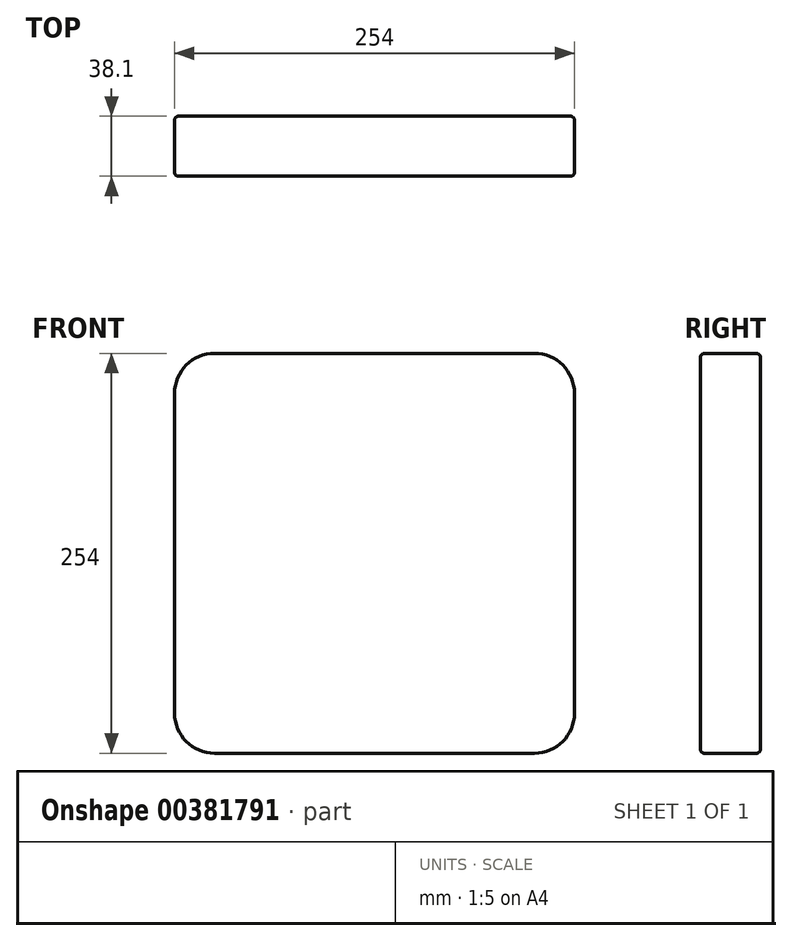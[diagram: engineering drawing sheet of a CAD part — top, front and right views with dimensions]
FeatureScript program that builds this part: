
annotation { "Feature Type Name" : "Feature", "Feature Type Description" : "" }
export const myFeature = defineFeature(function(context is Context, id is Id, definition is map)
    precondition{}
    {
        {
            var Q0;
            Q0=qCreatedBy(makeId("Front.planeOp"),FACE);
            var sketch = newSketch(context, id + "F0", { "sketchPlane" : qUnion([Q0])});
            skLineSegment(sketch, "E0.bottom", {"start": v(0, 0) * mm, "end": v(254, 0) * mm});
            skLineSegment(sketch, "E0.top", {"start": v(0, 254) * mm, "end": v(254, 254) * mm});
            skLineSegment(sketch, "E0.left", {"start": v(0, 0) * mm, "end": v(0, 254) * mm});
            skLineSegment(sketch, "E0.right", {"start": v(254, 0) * mm, "end": v(254, 254) * mm});
            skSolve(sketch);
        }
        {
            var Q0;
            Q0=makeQuery(id+"F0.imprint","IMPRINT",FACE,{"disambiguationData":[TD([[makeQuery(id+"F0.imprint","IMPRINT",EDGE,{"derivedFrom":sQuery(id+"F0.wireOp",EDGE,"E0.bottom")}),1.0]])]});
            extrude(context, id + "F1", {"entities" : qUnion([Q0]), "depth" : 38.1 * mm});
        }
        {
            var Q0;
            Q0=makeQuery(id+"F1.opExtrude","SWEPT_EDGE",EDGE,{"disambiguationData":[OSD([sQuery(id+"F0.wireOp",EDGE,"E0.top"),sQuery(id+"F0.wireOp",EDGE,"E0.left")])]});
            fillet(context, id + "F2", {"entities" : qUnion([Q0]), "radius" : 25.4 * mm, "tangentPropagation" : true, "allowEdgeOverflow" : false});
        }
        {
            var Q0;
            Q0=makeQuery(id+"F1.opExtrude","SWEPT_EDGE",EDGE,{"disambiguationData":[OSD([sQuery(id+"F0.wireOp",EDGE,"E0.bottom"),sQuery(id+"F0.wireOp",EDGE,"E0.left")])]});
            fillet(context, id + "F3", {"entities" : qUnion([Q0]), "radius" : 25.4 * mm, "tangentPropagation" : true, "allowEdgeOverflow" : false});
        }
        {
            var Q0;
            Q0=makeQuery(id+"F1.opExtrude","SWEPT_EDGE",EDGE,{"disambiguationData":[OSD([sQuery(id+"F0.wireOp",EDGE,"E0.bottom"),sQuery(id+"F0.wireOp",EDGE,"E0.right")])]});
            fillet(context, id + "F4", {"entities" : qUnion([Q0]), "radius" : 25.4 * mm, "tangentPropagation" : true, "allowEdgeOverflow" : false});
        }
        {
            var Q0;
            Q0=makeQuery(id+"F1.opExtrude","SWEPT_EDGE",EDGE,{"disambiguationData":[OSD([sQuery(id+"F0.wireOp",EDGE,"E0.top"),sQuery(id+"F0.wireOp",EDGE,"E0.right")])]});
            fillet(context, id + "F5", {"entities" : qUnion([Q0]), "radius" : 25.4 * mm, "tangentPropagation" : true, "allowEdgeOverflow" : false});
        }
        {
            var Q0;
            Q0=makeQuery(id+"F1.opExtrude","CAP_EDGE",EDGE,{"disambiguationData":[OSD([sQuery(id+"F0.wireOp",EDGE,"E0.top")])],"isStart":true});
            var Q1;
            {var subQ0=sQuery(id+"F0.wireOp",EDGE,"E0.right");var subQ1=sQuery(id+"F0.wireOp",EDGE,"E0.top");Q1=makeQuery(id+"F5.opFillet","BLEND_EDGE",EDGE,{"blendedFrom":[makeQuery(id+"F1.opExtrude","SWEPT_EDGE",EDGE,{"disambiguationData":[OSD([subQ1,subQ0])]}),makeQuery(id+"F1.opExtrude","CAP_FACE",FACE,{"disambiguationData":[OSD([sQuery(id+"F0.wireOp",EDGE,"E0.bottom"),subQ1,sQuery(id+"F0.wireOp",EDGE,"E0.left"),subQ0])],"isStart":true})],"blendedInto":[makeQuery(id+"F1.opExtrude","CAP_FACE",FACE,{"disambiguationData":[OSD([sQuery(id+"F0.wireOp",EDGE,"E0.bottom"),subQ1,sQuery(id+"F0.wireOp",EDGE,"E0.left"),subQ0])],"isStart":true})]});}
            var Q2;
            Q2=makeQuery(id+"F1.opExtrude","CAP_EDGE",EDGE,{"disambiguationData":[OSD([sQuery(id+"F0.wireOp",EDGE,"E0.right")])],"isStart":true});
            var Q3;
            {var subQ0=sQuery(id+"F0.wireOp",EDGE,"E0.right");var subQ1=sQuery(id+"F0.wireOp",EDGE,"E0.bottom");Q3=makeQuery(id+"F4.opFillet","BLEND_EDGE",EDGE,{"blendedFrom":[makeQuery(id+"F1.opExtrude","SWEPT_EDGE",EDGE,{"disambiguationData":[OSD([subQ1,subQ0])]}),makeQuery(id+"F1.opExtrude","CAP_FACE",FACE,{"disambiguationData":[OSD([subQ1,sQuery(id+"F0.wireOp",EDGE,"E0.top"),sQuery(id+"F0.wireOp",EDGE,"E0.left"),subQ0])],"isStart":true})],"blendedInto":[makeQuery(id+"F1.opExtrude","CAP_FACE",FACE,{"disambiguationData":[OSD([subQ1,sQuery(id+"F0.wireOp",EDGE,"E0.top"),sQuery(id+"F0.wireOp",EDGE,"E0.left"),subQ0])],"isStart":true})]});}
            var Q4;
            Q4=makeQuery(id+"F1.opExtrude","CAP_EDGE",EDGE,{"disambiguationData":[OSD([sQuery(id+"F0.wireOp",EDGE,"E0.bottom")])],"isStart":true});
            var Q5;
            {var subQ0=sQuery(id+"F0.wireOp",EDGE,"E0.left");var subQ1=sQuery(id+"F0.wireOp",EDGE,"E0.bottom");Q5=makeQuery(id+"F3.opFillet","BLEND_EDGE",EDGE,{"blendedFrom":[makeQuery(id+"F1.opExtrude","SWEPT_EDGE",EDGE,{"disambiguationData":[OSD([subQ1,subQ0])]}),makeQuery(id+"F1.opExtrude","CAP_FACE",FACE,{"disambiguationData":[OSD([subQ1,sQuery(id+"F0.wireOp",EDGE,"E0.top"),subQ0,sQuery(id+"F0.wireOp",EDGE,"E0.right")])],"isStart":true})],"blendedInto":[makeQuery(id+"F1.opExtrude","CAP_FACE",FACE,{"disambiguationData":[OSD([subQ1,sQuery(id+"F0.wireOp",EDGE,"E0.top"),subQ0,sQuery(id+"F0.wireOp",EDGE,"E0.right")])],"isStart":true})]});}
            var Q6;
            Q6=makeQuery(id+"F1.opExtrude","CAP_EDGE",EDGE,{"disambiguationData":[OSD([sQuery(id+"F0.wireOp",EDGE,"E0.left")])],"isStart":true});
            var Q7;
            {var subQ0=sQuery(id+"F0.wireOp",EDGE,"E0.left");var subQ1=sQuery(id+"F0.wireOp",EDGE,"E0.top");Q7=makeQuery(id+"F2.opFillet","BLEND_EDGE",EDGE,{"blendedFrom":[makeQuery(id+"F1.opExtrude","SWEPT_EDGE",EDGE,{"disambiguationData":[OSD([subQ1,subQ0])]}),makeQuery(id+"F1.opExtrude","CAP_FACE",FACE,{"disambiguationData":[OSD([sQuery(id+"F0.wireOp",EDGE,"E0.bottom"),subQ1,subQ0,sQuery(id+"F0.wireOp",EDGE,"E0.right")])],"isStart":true})],"blendedInto":[makeQuery(id+"F1.opExtrude","CAP_FACE",FACE,{"disambiguationData":[OSD([sQuery(id+"F0.wireOp",EDGE,"E0.bottom"),subQ1,subQ0,sQuery(id+"F0.wireOp",EDGE,"E0.right")])],"isStart":true})]});}
            fillet(context, id + "F6", {"entities" : qUnion([Q0, Q1, Q2, Q3, Q4, Q5, Q6, Q7]), "radius" : 2.54 * mm, "tangentPropagation" : true, "allowEdgeOverflow" : false});
        }
        {
            var Q0;
            {var subQ0=sQuery(id+"F0.wireOp",EDGE,"E0.right");var subQ1=sQuery(id+"F0.wireOp",EDGE,"E0.top");Q0=makeQuery(id+"F5.opFillet","BLEND_EDGE",EDGE,{"blendedFrom":[makeQuery(id+"F1.opExtrude","SWEPT_EDGE",EDGE,{"disambiguationData":[OSD([subQ1,subQ0])]}),makeQuery(id+"F1.opExtrude","CAP_FACE",FACE,{"disambiguationData":[OSD([sQuery(id+"F0.wireOp",EDGE,"E0.bottom"),subQ1,sQuery(id+"F0.wireOp",EDGE,"E0.left"),subQ0])],"isStart":false})],"blendedInto":[makeQuery(id+"F1.opExtrude","CAP_FACE",FACE,{"disambiguationData":[OSD([sQuery(id+"F0.wireOp",EDGE,"E0.bottom"),subQ1,sQuery(id+"F0.wireOp",EDGE,"E0.left"),subQ0])],"isStart":false})]});}
            var Q1;
            Q1=makeQuery(id+"F1.opExtrude","CAP_EDGE",EDGE,{"disambiguationData":[OSD([sQuery(id+"F0.wireOp",EDGE,"E0.right")])],"isStart":false});
            var Q2;
            Q2=makeQuery(id+"F1.opExtrude","CAP_EDGE",EDGE,{"disambiguationData":[OSD([sQuery(id+"F0.wireOp",EDGE,"E0.top")])],"isStart":false});
            var Q3;
            {var subQ0=sQuery(id+"F0.wireOp",EDGE,"E0.left");var subQ1=sQuery(id+"F0.wireOp",EDGE,"E0.top");Q3=makeQuery(id+"F2.opFillet","BLEND_EDGE",EDGE,{"blendedFrom":[makeQuery(id+"F1.opExtrude","SWEPT_EDGE",EDGE,{"disambiguationData":[OSD([subQ1,subQ0])]}),makeQuery(id+"F1.opExtrude","CAP_FACE",FACE,{"disambiguationData":[OSD([sQuery(id+"F0.wireOp",EDGE,"E0.bottom"),subQ1,subQ0,sQuery(id+"F0.wireOp",EDGE,"E0.right")])],"isStart":false})],"blendedInto":[makeQuery(id+"F1.opExtrude","CAP_FACE",FACE,{"disambiguationData":[OSD([sQuery(id+"F0.wireOp",EDGE,"E0.bottom"),subQ1,subQ0,sQuery(id+"F0.wireOp",EDGE,"E0.right")])],"isStart":false})]});}
            var Q4;
            Q4=makeQuery(id+"F1.opExtrude","CAP_EDGE",EDGE,{"disambiguationData":[OSD([sQuery(id+"F0.wireOp",EDGE,"E0.left")])],"isStart":false});
            var Q5;
            {var subQ0=sQuery(id+"F0.wireOp",EDGE,"E0.left");var subQ1=sQuery(id+"F0.wireOp",EDGE,"E0.bottom");Q5=makeQuery(id+"F3.opFillet","BLEND_EDGE",EDGE,{"blendedFrom":[makeQuery(id+"F1.opExtrude","SWEPT_EDGE",EDGE,{"disambiguationData":[OSD([subQ1,subQ0])]}),makeQuery(id+"F1.opExtrude","CAP_FACE",FACE,{"disambiguationData":[OSD([subQ1,sQuery(id+"F0.wireOp",EDGE,"E0.top"),subQ0,sQuery(id+"F0.wireOp",EDGE,"E0.right")])],"isStart":false})],"blendedInto":[makeQuery(id+"F1.opExtrude","CAP_FACE",FACE,{"disambiguationData":[OSD([subQ1,sQuery(id+"F0.wireOp",EDGE,"E0.top"),subQ0,sQuery(id+"F0.wireOp",EDGE,"E0.right")])],"isStart":false})]});}
            var Q6;
            Q6=makeQuery(id+"F1.opExtrude","CAP_EDGE",EDGE,{"disambiguationData":[OSD([sQuery(id+"F0.wireOp",EDGE,"E0.bottom")])],"isStart":false});
            var Q7;
            {var subQ0=sQuery(id+"F0.wireOp",EDGE,"E0.right");var subQ1=sQuery(id+"F0.wireOp",EDGE,"E0.bottom");Q7=makeQuery(id+"F4.opFillet","BLEND_EDGE",EDGE,{"blendedFrom":[makeQuery(id+"F1.opExtrude","SWEPT_EDGE",EDGE,{"disambiguationData":[OSD([subQ1,subQ0])]}),makeQuery(id+"F1.opExtrude","CAP_FACE",FACE,{"disambiguationData":[OSD([subQ1,sQuery(id+"F0.wireOp",EDGE,"E0.top"),sQuery(id+"F0.wireOp",EDGE,"E0.left"),subQ0])],"isStart":false})],"blendedInto":[makeQuery(id+"F1.opExtrude","CAP_FACE",FACE,{"disambiguationData":[OSD([subQ1,sQuery(id+"F0.wireOp",EDGE,"E0.top"),sQuery(id+"F0.wireOp",EDGE,"E0.left"),subQ0])],"isStart":false})]});}
            fillet(context, id + "F7", {"entities" : qUnion([Q0, Q1, Q2, Q3, Q4, Q5, Q6, Q7]), "radius" : 2.54 * mm, "tangentPropagation" : true, "allowEdgeOverflow" : false});
        }
    });
